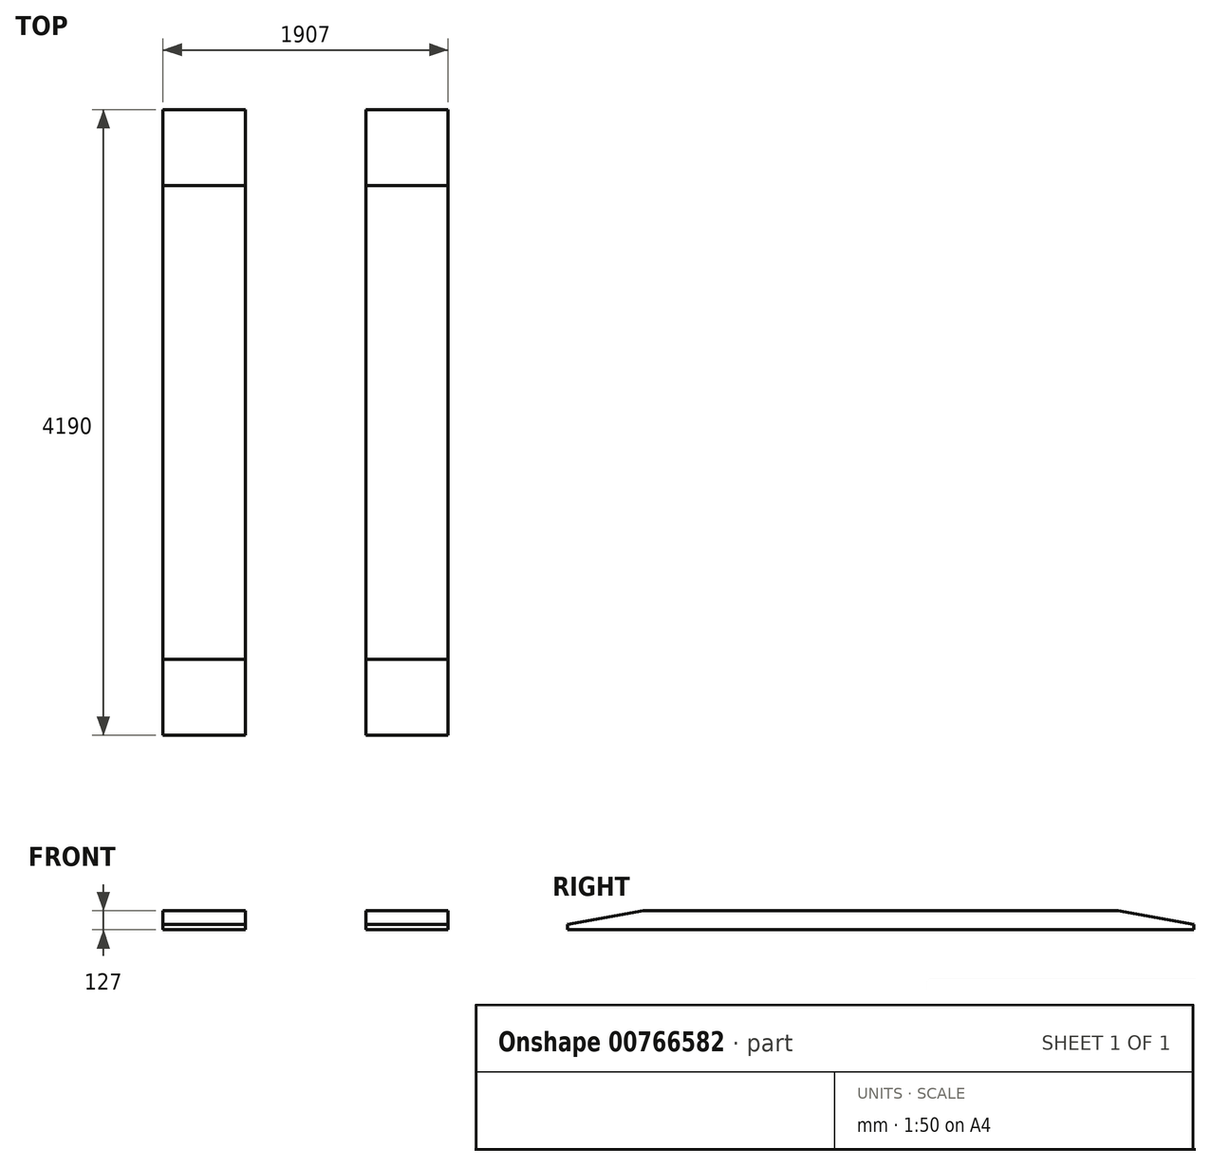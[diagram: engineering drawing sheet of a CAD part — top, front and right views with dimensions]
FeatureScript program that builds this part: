
annotation { "Feature Type Name" : "Feature", "Feature Type Description" : "" }
export const myFeature = defineFeature(function(context is Context, id is Id, definition is map)
    precondition{}
    {
        {
            var Q0;
            Q0=qCreatedBy(makeId("Top.planeOp"),FACE);
            var sketch = newSketch(context, id + "F0", { "sketchPlane" : qUnion([Q0])});
            skLineSegment(sketch, "E0.bottom", {"start": v(-953.5, -2095) * mm, "end": v(953.5, -2095) * mm});
            skLineSegment(sketch, "E0.top", {"start": v(-953.5, 2095) * mm, "end": v(953.5, 2095) * mm});
            skLineSegment(sketch, "E0.left", {"start": v(-953.5, -2095) * mm, "end": v(-953.5, 2095) * mm});
            skLineSegment(sketch, "E0.right", {"start": v(953.5, -2095) * mm, "end": v(953.5, 2095) * mm});
            skLineSegment(sketch, "E1", {"start": v(-953.5, 2095) * mm, "end": v(953.5, -2095) * mm});
            skSolve(sketch);
        }
        {
            var Q0;
            Q0 = qSketchRegion(id + "F0", true);
            extrude(context, id + "F1", {"entities" : qUnion([Q0]), "depth" : 127 * mm, "offsetDistance" : 25.4 * mm});
        }
        {
            var Q0;
            Q0=makeQuery(id+"F1.opExtrude","CAP_FACE",FACE,{"disambiguationData":[OSD([sQuery(id+"F0.wireOp",EDGE,"E0.bottom"),sQuery(id+"F0.wireOp",EDGE,"E0.top"),sQuery(id+"F0.wireOp",EDGE,"E0.left"),sQuery(id+"F0.wireOp",EDGE,"E0.right")])],"isStart":false});
            var sketch = newSketch(context, id + "F2", { "sketchPlane" : qUnion([Q0])});
            skLineSegment(sketch, "E2.bottom", {"start": v(-403.5, 2095) * mm, "end": v(403.5, 2095) * mm});
            skLineSegment(sketch, "E2.top", {"start": v(-403.5, -2095) * mm, "end": v(403.5, -2095) * mm});
            skLineSegment(sketch, "E2.left", {"start": v(-403.5, 2095) * mm, "end": v(-403.5, -2095) * mm});
            skLineSegment(sketch, "E2.right", {"start": v(403.5, 2095) * mm, "end": v(403.5, -2095) * mm});
            skLineSegment(sketch, "E3", {"start": v(-403.5, 2095) * mm, "end": v(403.5, -2095) * mm, "construction": true});
            skSolve(sketch);
        }
        {
            var Q0;
            Q0 = qSketchRegion(id + "F2", true);
            var Q1;
            Q1=sQuery(id+"F2.wireOp",EDGE,"E3");
            extrude(context, id + "F3", {"entities" : qUnion([Q0]), "operationType" : NewBodyOperationType.REMOVE, "surfaceEntities" : qUnion([Q1]), "endBound" : BoundingType.THROUGH_ALL, "oppositeDirection" : true, "depth" : 25.4 * mm, "offsetDistance" : 25.4 * mm});
        }
        {
            var Q0;
            {var subQ0=sQuery(id+"F0.wireOp",EDGE,"E0.bottom");var subQ1=sQuery(id+"F0.wireOp",EDGE,"E0.left");Q0=makeQuery(id+"F3.boolean.opBoolean","SPLIT",EDGE,{"disambiguationData":[TD([makeQuery(id+"F1.opExtrude","SWEPT_FACE",FACE,{"disambiguationData":[OSD([subQ1])]})])],"derivedFrom":makeQuery(id+"F1.opExtrude","CAP_EDGE",EDGE,{"disambiguationData":[OSD([subQ0])],"isStart":false})});}
            var Q1;
            {var subQ0=sQuery(id+"F0.wireOp",EDGE,"E0.bottom");var subQ1=sQuery(id+"F0.wireOp",EDGE,"E0.right");Q1=makeQuery(id+"F3.boolean.opBoolean","SPLIT",EDGE,{"disambiguationData":[TD([makeQuery(id+"F1.opExtrude","SWEPT_FACE",FACE,{"disambiguationData":[OSD([subQ1])]})])],"derivedFrom":makeQuery(id+"F1.opExtrude","CAP_EDGE",EDGE,{"disambiguationData":[OSD([subQ0])],"isStart":false})});}
            var Q2;
            {var subQ0=sQuery(id+"F0.wireOp",EDGE,"E0.right");var subQ1=sQuery(id+"F0.wireOp",EDGE,"E0.top");Q2=makeQuery(id+"F3.boolean.opBoolean","SPLIT",EDGE,{"disambiguationData":[TD([makeQuery(id+"F1.opExtrude","SWEPT_FACE",FACE,{"disambiguationData":[OSD([subQ0])]})])],"derivedFrom":makeQuery(id+"F1.opExtrude","CAP_EDGE",EDGE,{"disambiguationData":[OSD([subQ1])],"isStart":false})});}
            var Q3;
            {var subQ0=sQuery(id+"F0.wireOp",EDGE,"E0.left");var subQ1=sQuery(id+"F0.wireOp",EDGE,"E0.top");Q3=makeQuery(id+"F3.boolean.opBoolean","SPLIT",EDGE,{"disambiguationData":[TD([makeQuery(id+"F1.opExtrude","SWEPT_FACE",FACE,{"disambiguationData":[OSD([subQ0])]})])],"derivedFrom":makeQuery(id+"F1.opExtrude","CAP_EDGE",EDGE,{"disambiguationData":[OSD([subQ1])],"isStart":false})});}
            chamfer(context, id + "F4", {"entities" : qUnion([Q0, Q1, Q2, Q3]), "chamferType" : ChamferType.OFFSET_ANGLE, "width" : 508 * mm, "oppositeDirection" : false, "angle" : 10 * degree, "tangentPropagation" : true});
        }
    });
